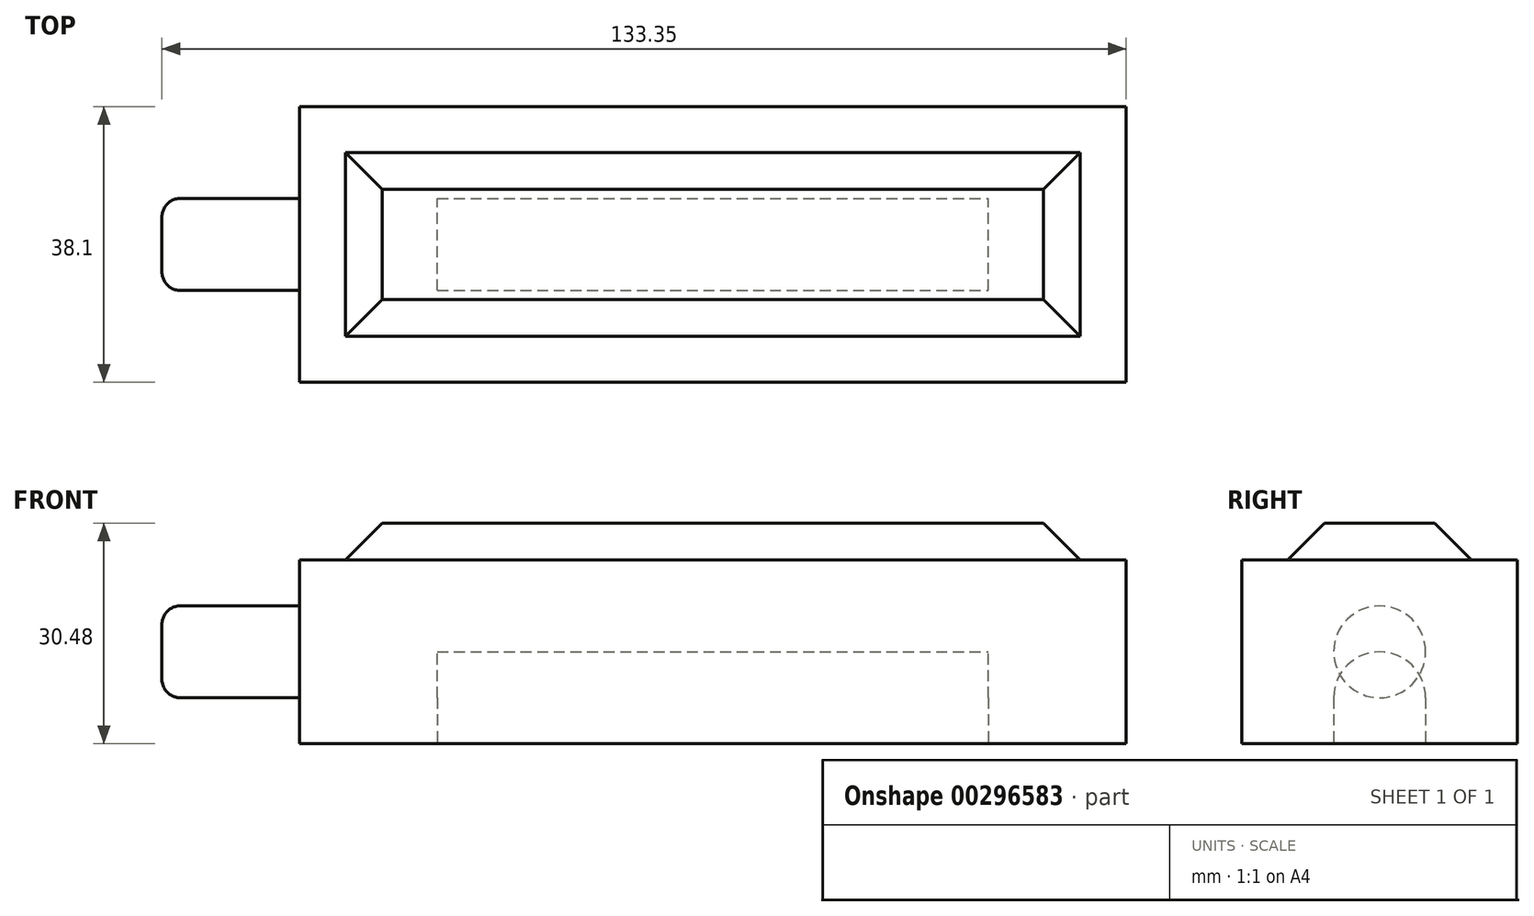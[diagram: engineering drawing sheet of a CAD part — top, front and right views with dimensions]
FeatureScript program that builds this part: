
annotation { "Feature Type Name" : "Feature", "Feature Type Description" : "" }
export const myFeature = defineFeature(function(context is Context, id is Id, definition is map)
    precondition{}
    {
        {
            var Q0;
            Q0=qCreatedBy(makeId("Top.planeOp"),FACE);
            var sketch = newSketch(context, id + "F0", { "sketchPlane" : qUnion([Q0])});
            skLineSegment(sketch, "E0.bottom", {"start": v(-57.15, 19.05) * mm, "end": v(57.15, 19.05) * mm});
            skLineSegment(sketch, "E0.top", {"start": v(-57.15, -19.05) * mm, "end": v(57.15, -19.05) * mm});
            skLineSegment(sketch, "E0.left", {"start": v(-57.15, 19.05) * mm, "end": v(-57.15, -19.05) * mm});
            skLineSegment(sketch, "E0.right", {"start": v(57.15, 19.05) * mm, "end": v(57.15, -19.05) * mm});
            skSolve(sketch);
        }
        {
            var Q0;
            Q0=makeQuery(id+"F0.imprint","IMPRINT",FACE,{"disambiguationData":[TD([[makeQuery(id+"F0.imprint","IMPRINT",EDGE,{"derivedFrom":sQuery(id+"F0.wireOp",EDGE,"E0.bottom")}),-1.0]])]});
            extrude(context, id + "F1", {"entities" : qUnion([Q0]), "depth" : 25.4 * mm});
        }
        {
            var Q0;
            Q0=makeQuery(id+"F1.opExtrude","SWEPT_FACE",FACE,{"disambiguationData":[OSD([sQuery(id+"F0.wireOp",EDGE,"E0.left")])]});
            var sketch = newSketch(context, id + "F2", { "sketchPlane" : qUnion([Q0])});
            skCircle(sketch, "E1", {"center": v(0, 12.7) * mm, "radius": 6.35 * mm});
            skSolve(sketch);
        }
        {
            var Q0;
            Q0=makeQuery(id+"F2.imprint","IMPRINT",FACE,{"disambiguationData":[TD([[makeQuery(id+"F2.imprint","IMPRINT",EDGE,{"derivedFrom":sQuery(id+"F2.wireOp",EDGE,"E1")}),1.0]])]});
            extrude(context, id + "F3", {"entities" : qUnion([Q0]), "operationType" : NewBodyOperationType.ADD, "depth" : 19.05 * mm});
        }
        {
            var Q0;
            Q0=makeQuery(id+"F3.opExtrude","CAP_EDGE",EDGE,{"disambiguationData":[OSD([sQuery(id+"F2.wireOp",EDGE,"E1")])],"isStart":false});
            fillet(context, id + "F4", {"entities" : qUnion([Q0]), "radius" : 2.54 * mm, "tangentPropagation" : true, "allowEdgeOverflow" : false});
        }
        {
            var Q0;
            Q0=makeQuery(id+"F1.opExtrude","CAP_FACE",FACE,{"disambiguationData":[OSD([sQuery(id+"F0.wireOp",EDGE,"E0.bottom"),sQuery(id+"F0.wireOp",EDGE,"E0.top"),sQuery(id+"F0.wireOp",EDGE,"E0.left"),sQuery(id+"F0.wireOp",EDGE,"E0.right")])],"isStart":false});
            var sketch = newSketch(context, id + "F5", { "sketchPlane" : qUnion([Q0])});
            skLineSegment(sketch, "E2.bottom", {"start": v(-50.8, 12.7) * mm, "end": v(50.8, 12.7) * mm});
            skLineSegment(sketch, "E2.top", {"start": v(-50.8, -12.7) * mm, "end": v(50.8, -12.7) * mm});
            skLineSegment(sketch, "E2.left", {"start": v(-50.8, 12.7) * mm, "end": v(-50.8, -12.7) * mm});
            skLineSegment(sketch, "E2.right", {"start": v(50.8, 12.7) * mm, "end": v(50.8, -12.7) * mm});
            skSolve(sketch);
        }
        {
            var Q0;
            Q0 = qSketchRegion(id + "F5", true);
            extrude(context, id + "F6", {"entities" : qUnion([Q0]), "operationType" : NewBodyOperationType.ADD, "depth" : 5.08 * mm});
        }
        {
            var Q0;
            Q0=makeQuery(id+"F6.opExtrude","CAP_EDGE",EDGE,{"disambiguationData":[OSD([sQuery(id+"F5.wireOp",EDGE,"E2.top")])],"isStart":false});
            var Q1;
            Q1=makeQuery(id+"F6.opExtrude","CAP_EDGE",EDGE,{"disambiguationData":[OSD([sQuery(id+"F5.wireOp",EDGE,"E2.left")])],"isStart":false});
            var Q2;
            Q2=makeQuery(id+"F6.opExtrude","CAP_EDGE",EDGE,{"disambiguationData":[OSD([sQuery(id+"F5.wireOp",EDGE,"E2.right")])],"isStart":false});
            var Q3;
            Q3=makeQuery(id+"F6.opExtrude","CAP_EDGE",EDGE,{"disambiguationData":[OSD([sQuery(id+"F5.wireOp",EDGE,"E2.bottom")])],"isStart":false});
            chamfer(context, id + "F7", {"entities" : qUnion([Q0, Q1, Q2, Q3]), "width" : 5.08 * mm, "tangentPropagation" : true});
        }
        {
            var Q0;
            Q0=makeQuery(id+"F1.opExtrude","CAP_FACE",FACE,{"disambiguationData":[OSD([sQuery(id+"F0.wireOp",EDGE,"E0.bottom"),sQuery(id+"F0.wireOp",EDGE,"E0.top"),sQuery(id+"F0.wireOp",EDGE,"E0.left"),sQuery(id+"F0.wireOp",EDGE,"E0.right")])],"isStart":true});
            var sketch = newSketch(context, id + "F8", { "sketchPlane" : qUnion([Q0])});
            skLineSegment(sketch, "E3.bottom", {"start": v(-38.1, 6.35) * mm, "end": v(38.1, 6.35) * mm});
            skLineSegment(sketch, "E3.top", {"start": v(-38.1, -6.35) * mm, "end": v(38.1, -6.35) * mm});
            skLineSegment(sketch, "E3.left", {"start": v(-38.1, 6.35) * mm, "end": v(-38.1, -6.35) * mm});
            skLineSegment(sketch, "E3.right", {"start": v(38.1, 6.35) * mm, "end": v(38.1, -6.35) * mm});
            skSolve(sketch);
        }
        {
            var Q0;
            Q0=makeQuery(id+"F8.imprint","IMPRINT",FACE,{"disambiguationData":[TD([[makeQuery(id+"F8.imprint","IMPRINT",EDGE,{"derivedFrom":sQuery(id+"F8.wireOp",EDGE,"E3.bottom")}),-1.0]])]});
            extrude(context, id + "F9", {"entities" : qUnion([Q0]), "operationType" : NewBodyOperationType.REMOVE, "oppositeDirection" : true, "depth" : 12.7 * mm});
        }
        {
            var Q0;
            Q0=makeQuery(id+"F9.boolean.opBoolean","COPY",EDGE,{"derivedFrom":makeQuery(id+"F9.opExtrude","CAP_EDGE",EDGE,{"disambiguationData":[OSD([sQuery(id+"F8.wireOp",EDGE,"E3.top")])],"isStart":false})});
            var Q1;
            Q1=makeQuery(id+"F9.boolean.opBoolean","COPY",EDGE,{"derivedFrom":makeQuery(id+"F9.opExtrude","CAP_EDGE",EDGE,{"disambiguationData":[OSD([sQuery(id+"F8.wireOp",EDGE,"E3.bottom")])],"isStart":false})});
            fillet(context, id + "F10", {"entities" : qUnion([Q0, Q1]), "radius" : 6.35 * mm, "tangentPropagation" : true, "allowEdgeOverflow" : false});
        }
    });
